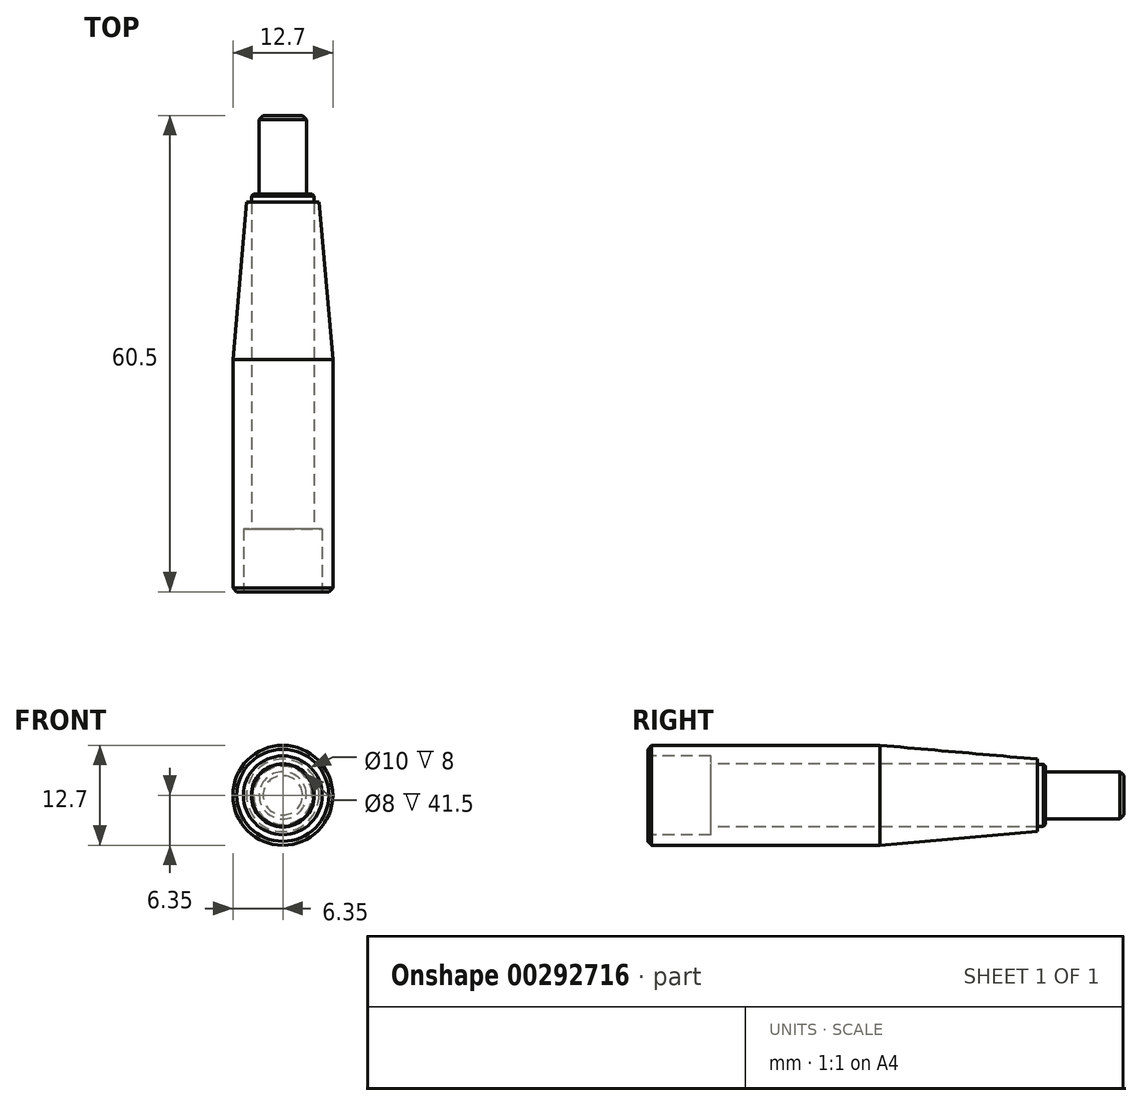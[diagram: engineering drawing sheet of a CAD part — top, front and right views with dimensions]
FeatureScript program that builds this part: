
annotation { "Feature Type Name" : "Feature", "Feature Type Description" : "" }
export const myFeature = defineFeature(function(context is Context, id is Id, definition is map)
    precondition{}
    {
        {
            var Q0;
            Q0=qCreatedBy(makeId("Front.planeOp"),FACE);
            var sketch = newSketch(context, id + "F0", { "sketchPlane" : qUnion([Q0])});
            skCircle(sketch, "E0", {"center": v(0, 0) * mm, "radius": 5 * mm});
            skSolve(sketch);
        }
        {
            var Q0;
            Q0=qSketchRegion(id+"F0",true);
            extrude(context, id + "F1", {"entities" : qUnion([Q0]), "oppositeDirection" : true, "depth" : 8 * mm});
        }
        {
            var Q0;
            Q0=makeQuery(id+"F1.opExtrude","CAP_FACE",FACE,{"disambiguationData":[OSD([sQuery(id+"F0.wireOp",EDGE,"E0")])],"isStart":true});
            var sketch = newSketch(context, id + "F2", { "sketchPlane" : qUnion([Q0])});
            skCircle(sketch, "E1.cCircle", {"center": v(0, 0) * mm, "radius": 3 * mm, "construction": true});
            skLineSegment(sketch, "E1.0", {"start": v(0, 3.46) * mm, "end": v(3, 1.73) * mm});
            skLineSegment(sketch, "E1.1", {"start": v(3, 1.73) * mm, "end": v(3, -1.73) * mm});
            skLineSegment(sketch, "E1.2", {"start": v(3, -1.73) * mm, "end": v(0, -3.46) * mm});
            skLineSegment(sketch, "E1.3", {"start": v(0, -3.46) * mm, "end": v(-3, -1.73) * mm});
            skLineSegment(sketch, "E1.4", {"start": v(-3, -1.73) * mm, "end": v(-3, 1.73) * mm});
            skLineSegment(sketch, "E1.5", {"start": v(-3, 1.73) * mm, "end": v(0, 3.46) * mm});
            skPoint(sketch, "E1.0.midPoint", {"position": v(1.5, 2.6) * mm});
            skSolve(sketch);
        }
        {
            var Q0;
            Q0=qSketchRegion(id+"F2",true);
            extrude(context, id + "F3", {"entities" : qUnion([Q0]), "operationType" : NewBodyOperationType.REMOVE, "oppositeDirection" : true, "depth" : 5 * mm});
        }
        {
            var Q0;
            Q0=makeQuery(id+"F3.boolean.opBoolean","COPY",FACE,{"derivedFrom":makeQuery(id+"F3.opExtrude","CAP_FACE",FACE,{"disambiguationData":[OSD([sQuery(id+"F2.wireOp",EDGE,"E1.0"),sQuery(id+"F2.wireOp",EDGE,"E1.1"),sQuery(id+"F2.wireOp",EDGE,"E1.2"),sQuery(id+"F2.wireOp",EDGE,"E1.3"),sQuery(id+"F2.wireOp",EDGE,"E1.4"),sQuery(id+"F2.wireOp",EDGE,"E1.5")])],"isStart":false})});
            var Q1;
            Q1=makeQuery(id+"F3.boolean.opBoolean","COPY",FACE,{"derivedFrom":makeQuery(id+"F3.opExtrude","SWEPT_FACE",FACE,{"disambiguationData":[OSD([sQuery(id+"F2.wireOp",EDGE,"E1.5")])]})});
            var Q2;
            Q2=makeQuery(id+"F3.boolean.opBoolean","COPY",FACE,{"derivedFrom":makeQuery(id+"F3.opExtrude","SWEPT_FACE",FACE,{"disambiguationData":[OSD([sQuery(id+"F2.wireOp",EDGE,"E1.2")])]})});
            fillet(context, id + "F4", {"entities" : qUnion([Q0, Q1, Q2]), "radius" : .5 * mm, "tangentPropagation" : true, "allowEdgeOverflow" : false});
        }
        {
            var Q0;
            Q0=makeQuery(id+"F1.opExtrude","CAP_FACE",FACE,{"disambiguationData":[OSD([sQuery(id+"F0.wireOp",EDGE,"E0")])],"isStart":false});
            var sketch = newSketch(context, id + "F5", { "sketchPlane" : qUnion([Q0])});
            skCircle(sketch, "E2", {"center": v(0, 0) * mm, "radius": 3.95 * mm});
            skSolve(sketch);
        }
        {
            var Q0;
            Q0=qSketchRegion(id+"F5",true);
            extrude(context, id + "F6", {"entities" : qUnion([Q0]), "operationType" : NewBodyOperationType.ADD, "depth" : 42.5 * mm});
        }
        {
            var Q0;
            Q0=makeQuery(id+"F6.opExtrude","CAP_FACE",FACE,{"disambiguationData":[OSD([sQuery(id+"F5.wireOp",EDGE,"E2")])],"isStart":false});
            var sketch = newSketch(context, id + "F7", { "sketchPlane" : qUnion([Q0])});
            skCircle(sketch, "E3", {"center": v(0, 0) * mm, "radius": 3 * mm});
            skSolve(sketch);
        }
        {
            var Q0;
            Q0=qSketchRegion(id+"F7",true);
            extrude(context, id + "F8", {"entities" : qUnion([Q0]), "operationType" : NewBodyOperationType.ADD, "depth" : 10 * mm});
        }
        {
            var Q0;
            Q0=makeQuery(id+"F1.opExtrude","CAP_FACE",FACE,{"disambiguationData":[OSD([sQuery(id+"F0.wireOp",EDGE,"E0")])],"isStart":true});
            var sketch = newSketch(context, id + "F9", { "sketchPlane" : qUnion([Q0])});
            skCircle(sketch, "E4", {"center": v(0, 0) * mm, "radius": 6.35 * mm});
            skSolve(sketch);
        }
        {
            var Q0;
            Q0=qSketchRegion(id+"F9",true);
            extrude(context, id + "F10", {"entities" : qUnion([Q0]), "oppositeDirection" : true, "depth" : 29.5 * mm});
        }
        {
            var Q0;
            Q0=makeQuery(id+"F10.opExtrude","CAP_FACE",FACE,{"disambiguationData":[OSD([sQuery(id+"F9.wireOp",EDGE,"E4")])],"isStart":true});
            var sketch = newSketch(context, id + "F11", { "sketchPlane" : qUnion([Q0])});
            skCircle(sketch, "E5", {"center": v(0, 0) * mm, "radius": 5 * mm});
            skSolve(sketch);
        }
        {
            var Q0;
            Q0=qSketchRegion(id+"F11",true);
            extrude(context, id + "F12", {"entities" : qUnion([Q0]), "operationType" : NewBodyOperationType.REMOVE, "oppositeDirection" : true, "depth" : 8 * mm});
        }
        {
            var Q0;
            Q0=makeQuery(id+"F10.opExtrude","CAP_FACE",FACE,{"disambiguationData":[OSD([sQuery(id+"F9.wireOp",EDGE,"E4")])],"isStart":false});
            var sketch = newSketch(context, id + "F13", { "sketchPlane" : qUnion([Q0])});
            skCircle(sketch, "E6", {"center": v(0, 0) * mm, "radius": 6.35 * mm});
            skSolve(sketch);
        }
        {
            var Q0;
            Q0=qSketchRegion(id+"F13",true);
            extrude(context, id + "F14", {"entities" : qUnion([Q0]), "operationType" : NewBodyOperationType.ADD, "depth" : 20 * mm, "hasDraft" : true, "draftAngle" : 5 * degree, "draftPullDirection" : true});
        }
        {
            var Q0;
            Q0=makeQuery(id+"F12.boolean.opBoolean","COPY",FACE,{"derivedFrom":makeQuery(id+"F12.opExtrude","CAP_FACE",FACE,{"disambiguationData":[OSD([sQuery(id+"F11.wireOp",EDGE,"E5")])],"isStart":false})});
            var sketch = newSketch(context, id + "F15", { "sketchPlane" : qUnion([Q0])});
            skCircle(sketch, "E7", {"center": v(0, 0) * mm, "radius": 4 * mm});
            skSolve(sketch);
        }
        {
            var Q0;
            Q0=qSketchRegion(id+"F15",true);
            var Q1;
            Q1=makeQuery(id+"F14.opExtrude","CAP_FACE",FACE,{"disambiguationData":[OSD([sQuery(id+"F13.wireOp",EDGE,"E6")])],"isStart":false});
            extrude(context, id + "F16", {"entities" : qUnion([Q0]), "operationType" : NewBodyOperationType.REMOVE, "endBound" : BoundingType.UP_TO_SURFACE, "oppositeDirection" : true, "endBoundEntityFace" : qUnion([Q1]), "depth" : 25 * mm});
        }
        {
            var Q0;
            Q0=makeQuery(id+"F8.opExtrude","CAP_FACE",FACE,{"disambiguationData":[OSD([sQuery(id+"F7.wireOp",EDGE,"E3")])],"isStart":false});
            chamfer(context, id + "F17", {"entities" : qUnion([Q0]), "width" : .5 * mm, "tangentPropagation" : true});
        }
        {
            var Q0;
            Q0=makeQuery(id+"F6.opExtrude","CAP_EDGE",EDGE,{"disambiguationData":[OSD([sQuery(id+"F5.wireOp",EDGE,"E2")])],"isStart":false});
            chamfer(context, id + "F18", {"entities" : qUnion([Q0]), "width" : .25 * mm, "tangentPropagation" : true});
        }
        {
            var Q0;
            Q0=makeQuery(id+"F10.opExtrude","CAP_EDGE",EDGE,{"disambiguationData":[OSD([sQuery(id+"F9.wireOp",EDGE,"E4")])],"isStart":true});
            chamfer(context, id + "F19", {"entities" : qUnion([Q0]), "width" : .5 * mm, "tangentPropagation" : true});
        }
    });
